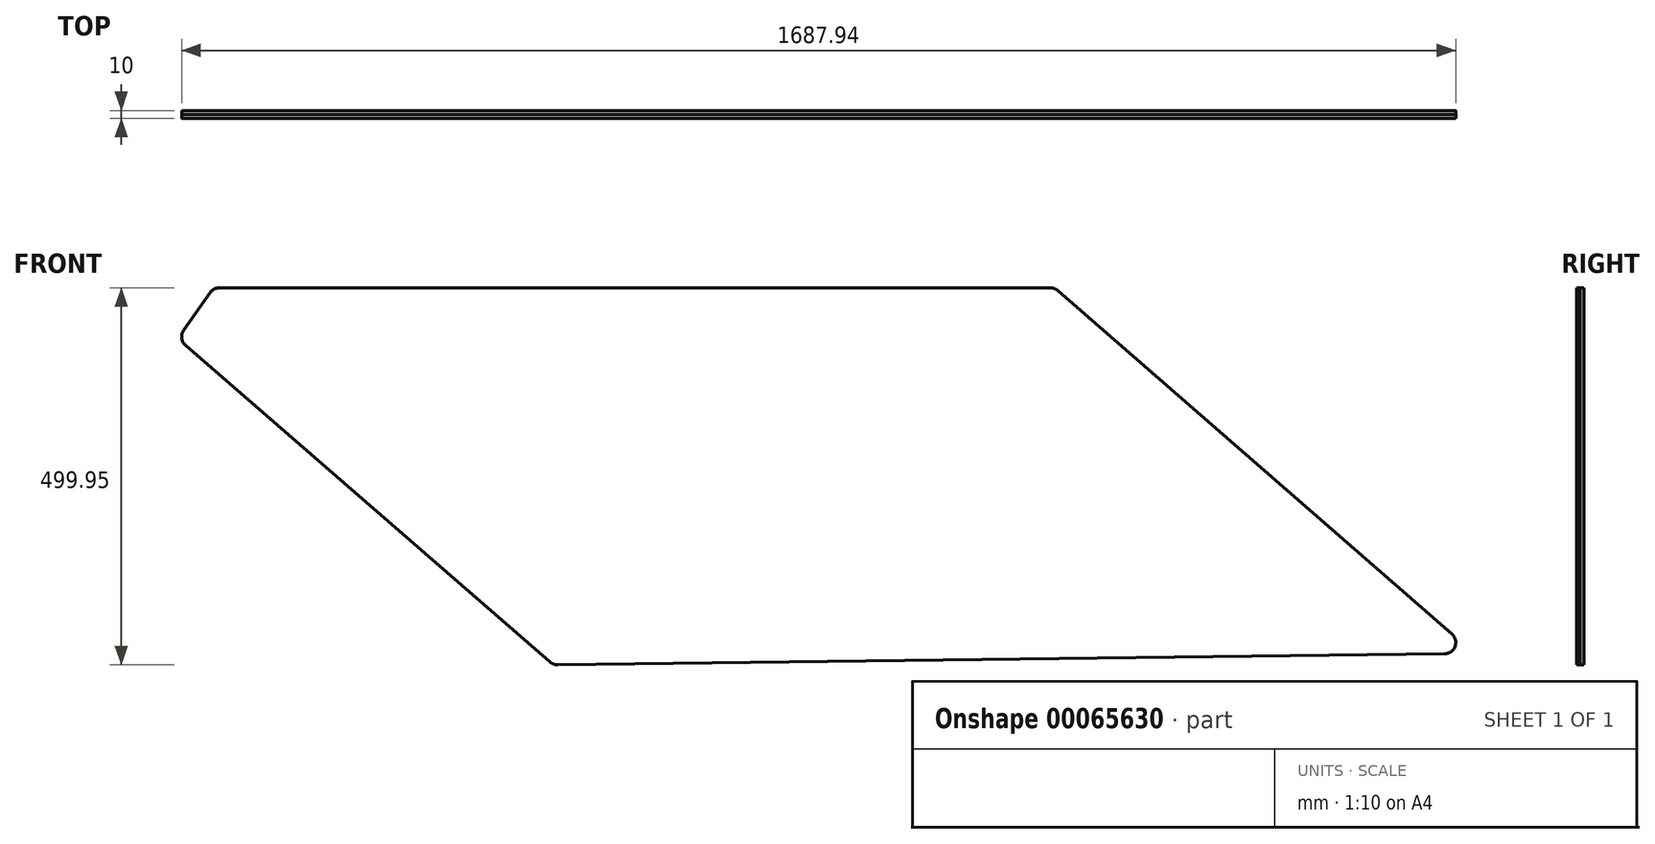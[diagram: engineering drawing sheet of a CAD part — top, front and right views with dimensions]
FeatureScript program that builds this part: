
annotation { "Feature Type Name" : "Feature", "Feature Type Description" : "" }
export const myFeature = defineFeature(function(context is Context, id is Id, definition is map)
    precondition{}
    {
        {
            var Q0;
            Q0=qCreatedBy(makeId("Front.planeOp"),FACE);
            var sketch = newSketch(context, id + "F0", { "sketchPlane" : qUnion([Q0])});
            skLineSegment(sketch, "E0", {"start": v(-344.93, 491.3) * mm, "end": v(765.07, 491.3) * mm});
            skLineSegment(sketch, "E1", {"start": v(765.07, 491.3) * mm, "end": v(1309.65, 16.3) * mm});
            skLineSegment(sketch, "E2", {"start": v(1309.65, 16.3) * mm, "end": v(104.74, 1.3) * mm});
            skPoint(sketch, "E3.visualSharp", {"position": v(0, 0) * mm});
            skLineSegment(sketch, "E4", {"start": v(-387.95, 429.87) * mm, "end": v(104.74, 1.3) * mm});
            skLineSegment(sketch, "E5", {"start": v(-387.95, 429.87) * mm, "end": v(-344.93, 491.3) * mm});
            skLineSegment(sketch, "E6.0", {"start": v(-347.53, 496.3) * mm, "end": v(766.94, 496.3) * mm});
            skLineSegment(sketch, "E6.1", {"start": v(-394.63, 429.05) * mm, "end": v(-347.53, 496.3) * mm});
            skLineSegment(sketch, "E6.2", {"start": v(766.94, 496.3) * mm, "end": v(1322.8, 11.47) * mm});
            skLineSegment(sketch, "E6.3", {"start": v(1322.8, 11.47) * mm, "end": v(102.9, -3.72) * mm});
            skLineSegment(sketch, "E6.4", {"start": v(-394.63, 429.05) * mm, "end": v(102.9, -3.72) * mm});
            skSolve(sketch);
        }
        {
            var Q0;
            Q0 = qSketchRegion(id + "F0", true);
            var Q1;
            Q1=makeQuery(id+"F0.imprint","IMPRINT",FACE,{"disambiguationData":[TD([[makeQuery(id+"F0.imprint","IMPRINT",EDGE,{"derivedFrom":sQuery(id+"F0.wireOp",EDGE,"E0")}),-1.0]])]});
            extrude(context, id + "F1", {"entities" : qUnion([Q0, Q1]), "depth" : 5 * mm});
        }
        {
            var Q0;
            Q0=makeQuery(id+"F1.opExtrude","SWEPT_EDGE",EDGE,{"disambiguationData":[OSD([sQuery(id+"F0.wireOp",EDGE,"E6.0"),sQuery(id+"F0.wireOp",EDGE,"E6.1")])]});
            var Q1;
            Q1=makeQuery(id+"F1.opExtrude","SWEPT_EDGE",EDGE,{"disambiguationData":[OSD([sQuery(id+"F0.wireOp",EDGE,"E6.1"),sQuery(id+"F0.wireOp",EDGE,"E6.4")])]});
            var Q2;
            Q2=makeQuery(id+"F1.opExtrude","SWEPT_EDGE",EDGE,{"disambiguationData":[OSD([sQuery(id+"F0.wireOp",EDGE,"E6.3"),sQuery(id+"F0.wireOp",EDGE,"E6.4")])]});
            var Q3;
            Q3=makeQuery(id+"F1.opExtrude","SWEPT_EDGE",EDGE,{"disambiguationData":[OSD([sQuery(id+"F0.wireOp",EDGE,"E6.2"),sQuery(id+"F0.wireOp",EDGE,"E6.3")])]});
            var Q4;
            Q4=makeQuery(id+"F1.opExtrude","SWEPT_EDGE",EDGE,{"disambiguationData":[OSD([sQuery(id+"F0.wireOp",EDGE,"E6.0"),sQuery(id+"F0.wireOp",EDGE,"E6.2")])]});
            fillet(context, id + "F2", {"entities" : qUnion([Q0, Q1, Q2, Q3, Q4]), "radius" : 15 * mm, "tangentPropagation" : true, "allowEdgeOverflow" : false});
        }
        {
            var Q0;
            Q0=makeQuery(id+"F1.opExtrude","SWEPT_BODY",BODY,{"disambiguationData":[OSD([sQuery(id+"F0.wireOp",EDGE,"E6.0"),sQuery(id+"F0.wireOp",EDGE,"E6.1"),sQuery(id+"F0.wireOp",EDGE,"E6.2"),sQuery(id+"F0.wireOp",EDGE,"E6.3"),sQuery(id+"F0.wireOp",EDGE,"E6.4")])]});
            var Q1;
            Q1=qCreatedBy(makeId("Front.planeOp"),FACE);
            mirror(context, id + "F3", {"entities" : qUnion([Q0]), "mirrorPlane" : qUnion([Q1])});
        }
    });
